# Revit family: FU_Chair_Sandler_Zenpro 0120
name_source: partatom
category: Furniture
units: mm (PartAtom-declared; Revit-internal decimal feet)

## family parameters
Always vertical = Yes
Cut with Voids When Loaded = No
OmniClass Number = 23.40.20.00
OmniClass Title = General Furniture and Specialties
Render Appearance Source = Family Geometry
Room Calculation Point = No
Shared = No
Work Plane-Based = No

## types (1)
- Zenpro 0120
    Default Elevation = 0 mm  [stored 0 ft]
    Depth = 640 mm  [stored 2.09974 ft]
    Description = Swivel task chair with horizontal stitching across the backrest. This heigh-adjustable chair has soft-tread casters and a weight-activated, synchronized tilt mechanism. Able to lock in four different positions and can be fine-tuned with the tension control knob. Designed by Mario Ruiz.

Greenguard Gold-certified to minimize the impact on indoor air quality. A sustainable chair that is 99% recyclable and made of 42% recycled materials.
    Height = 1277 mm
    Manufacturer = Sandler
    Model = Zenpro 0120
    URL = https://www.sandlerseating.com
    Width = 680 mm  [stored 2.23097 ft]

note: [stored X ft] marks values corroborated as IEEE doubles in the binary element streams (Revit-internal decimal feet)

## geometry (parser evidence)
native form markers: Sweep x8
no freeform markers — native parametric forms only
